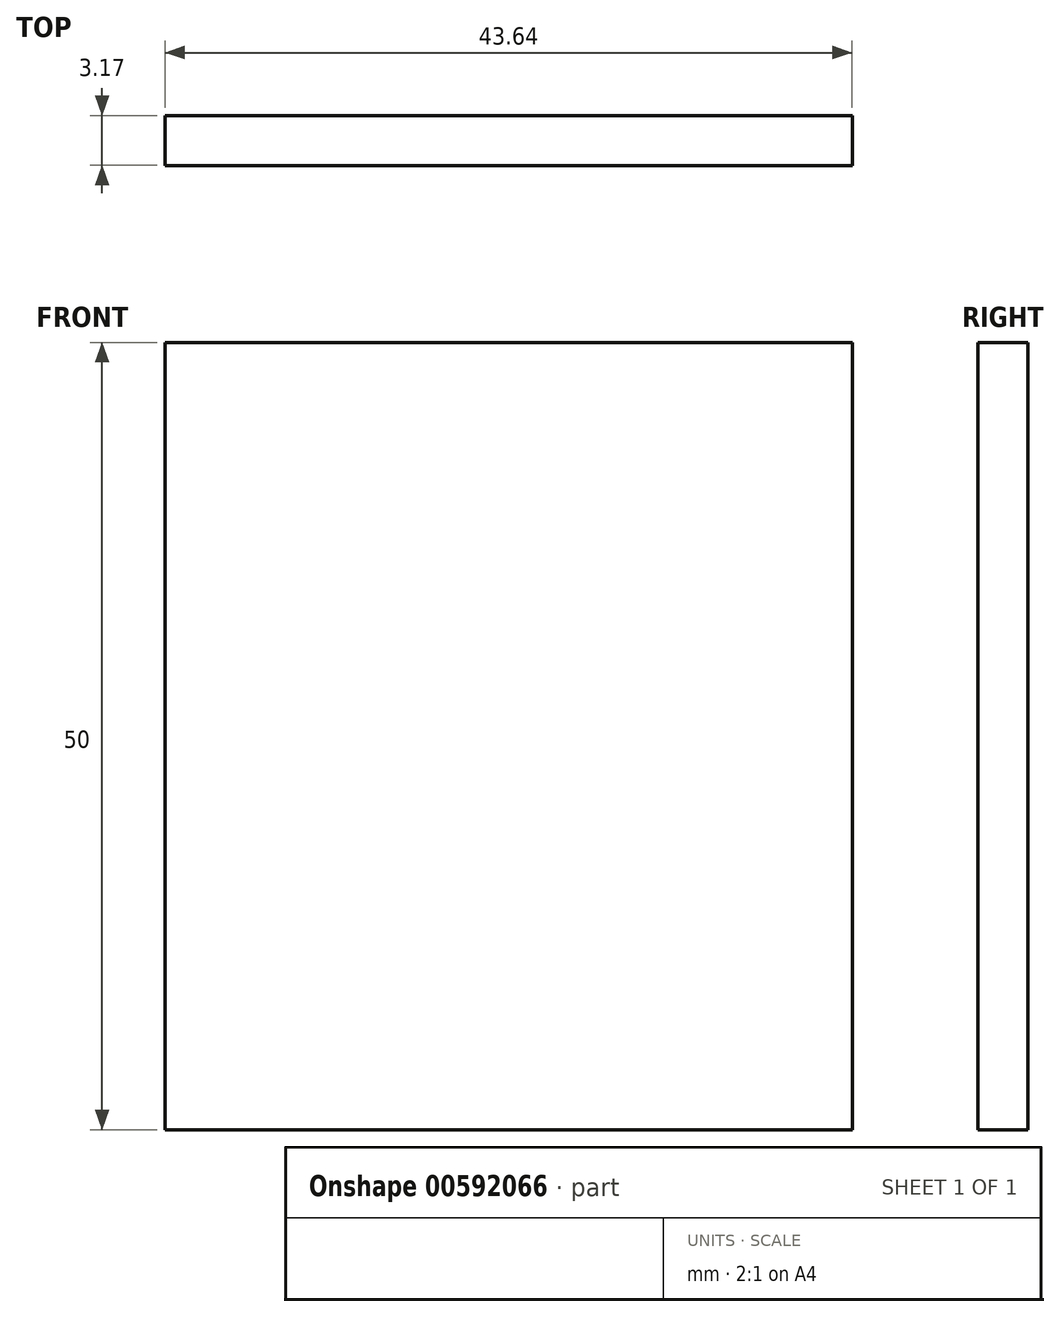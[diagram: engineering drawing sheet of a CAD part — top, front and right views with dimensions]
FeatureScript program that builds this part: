
annotation { "Feature Type Name" : "Feature", "Feature Type Description" : "" }
export const myFeature = defineFeature(function(context is Context, id is Id, definition is map)
    precondition{}
    {
        {
            var Q0;
            Q0=qCreatedBy(makeId("Front.planeOp"),FACE);
            var sketch = newSketch(context, id + "F0", { "sketchPlane" : qUnion([Q0])});
            skLineSegment(sketch, "E0.bottom", {"start": v(-21.83, 25) * mm, "end": v(21.83, 25) * mm});
            skLineSegment(sketch, "E0.top", {"start": v(-21.83, -25) * mm, "end": v(21.83, -25) * mm});
            skLineSegment(sketch, "E0.left", {"start": v(-21.82, 25) * mm, "end": v(-21.82, -25) * mm});
            skLineSegment(sketch, "E0.right", {"start": v(21.83, 25) * mm, "end": v(21.82, -25) * mm});
            skLineSegment(sketch, "E1", {"start": v(21.82, 0) * mm, "end": v(-21.82, 0) * mm, "construction": true});
            skLineSegment(sketch, "E2", {"start": v(0, 25) * mm, "end": v(0, -25) * mm, "construction": true});
            skSolve(sketch);
        }
        {
            var Q0;
            Q0=qSketchRegion(id+"F0",true);
            extrude(context, id + "F1", {"entities" : qUnion([Q0]), "depth" : 3.17 * mm, "offsetDistance" : 25 * mm});
        }
    });
